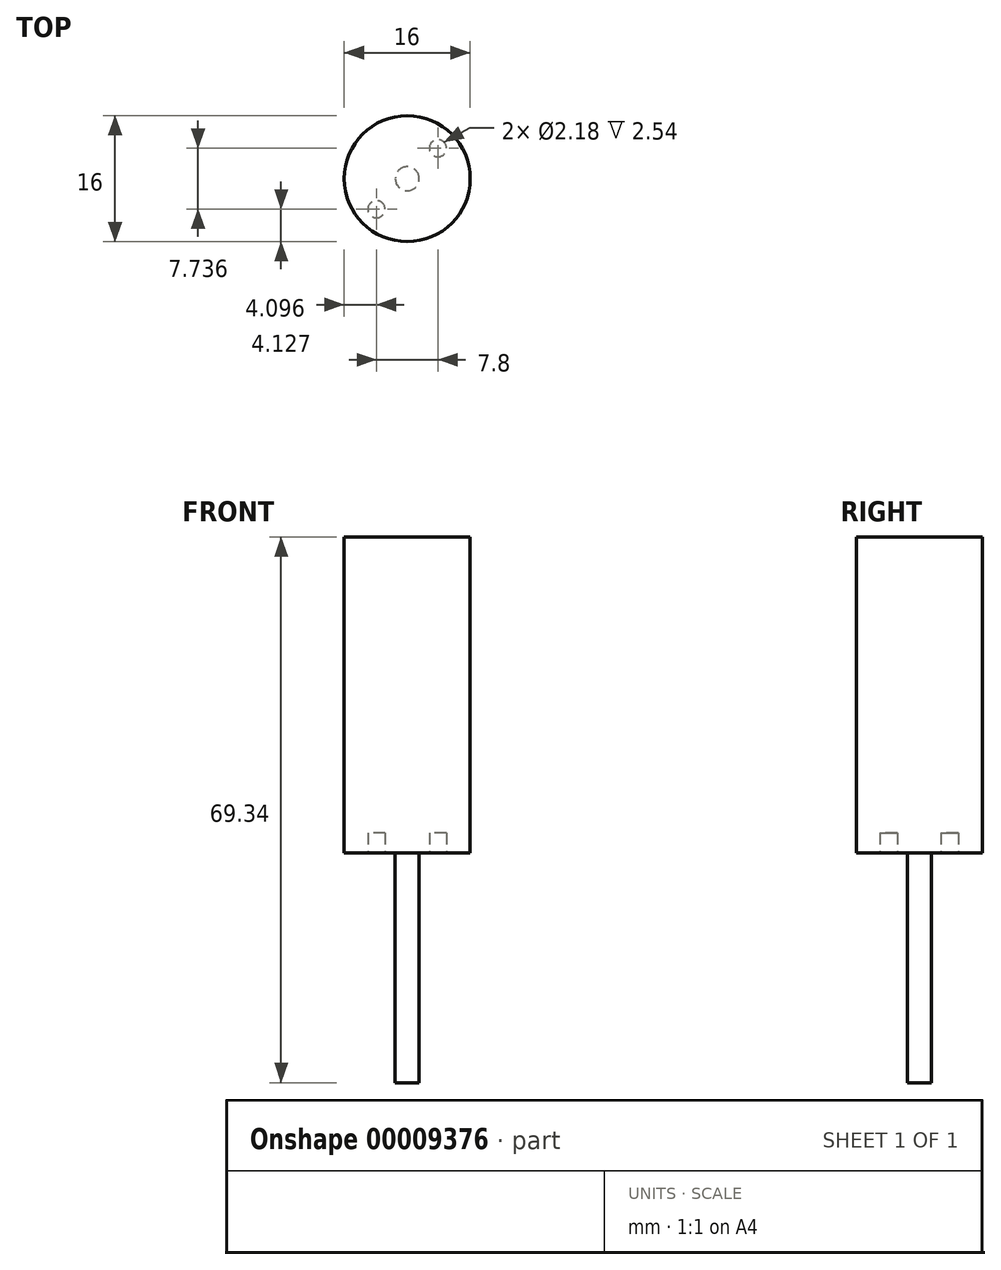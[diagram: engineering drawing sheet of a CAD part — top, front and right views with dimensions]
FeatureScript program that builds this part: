
annotation { "Feature Type Name" : "Feature", "Feature Type Description" : "" }
export const myFeature = defineFeature(function(context is Context, id is Id, definition is map)
    precondition{}
    {
        {
            var Q0;
            Q0=qCreatedBy(makeId("Top.planeOp"),FACE);
            var sketch = newSketch(context, id + "F0", { "sketchPlane" : qUnion([Q0])});
            skCircle(sketch, "E0", {"center": v(0, 0) * mm, "radius": 8 * mm});
            skCircle(sketch, "E1", {"center": v(-3.9, -3.87) * mm, "radius": 1.1 * mm});
            skCircle(sketch, "E2", {"center": v(3.9, 3.86) * mm, "radius": 1.1 * mm});
            skSolve(sketch);
        }
        {
            var Q0;
            Q0=makeQuery(id+"F0.imprint","IMPRINT",FACE,{"disambiguationData":[TD([[makeQuery(id+"F0.imprint","IMPRINT",EDGE,{"derivedFrom":sQuery(id+"F0.wireOp",EDGE,"E1")}),1.0]])]});
            var Q1;
            Q1=makeQuery(id+"F0.imprint","IMPRINT",FACE,{"disambiguationData":[TD([[makeQuery(id+"F0.imprint","IMPRINT",EDGE,{"derivedFrom":sQuery(id+"F0.wireOp",EDGE,"E2")}),1.0]])]});
            var Q2;
            Q2=makeQuery(id+"F0.imprint","IMPRINT",FACE,{"disambiguationData":[TD([[makeQuery(id+"F0.imprint","IMPRINT",EDGE,{"derivedFrom":sQuery(id+"F0.wireOp",EDGE,"E0")}),1.0]])]});
            extrude(context, id + "F1", {"entities" : qUnion([Q0, Q1, Q2]), "depth" : 40.13 * mm});
        }
        {
            var Q0;
            Q0=makeQuery(id+"F0.imprint","IMPRINT",FACE,{"disambiguationData":[TD([[makeQuery(id+"F0.imprint","IMPRINT",EDGE,{"derivedFrom":sQuery(id+"F0.wireOp",EDGE,"E2")}),1.0]])]});
            var Q1;
            Q1=makeQuery(id+"F0.imprint","IMPRINT",FACE,{"disambiguationData":[TD([[makeQuery(id+"F0.imprint","IMPRINT",EDGE,{"derivedFrom":sQuery(id+"F0.wireOp",EDGE,"E1")}),1.0]])]});
            extrude(context, id + "F2", {"entities" : qUnion([Q0, Q1]), "operationType" : NewBodyOperationType.REMOVE, "depth" : 2.54 * mm});
        }
        {
            var Q0;
            Q0=makeQuery(id+"F0.imprint","IMPRINT",FACE,{"disambiguationData":[TD([[makeQuery(id+"F0.imprint","IMPRINT",EDGE,{"derivedFrom":sQuery(id+"F0.wireOp",EDGE,"E0")}),1.0]])]});
            var sketch = newSketch(context, id + "F3", { "sketchPlane" : qUnion([Q0])});
            skCircle(sketch, "E3", {"center": v(0, 0) * mm, "radius": 1.52 * mm});
            skSolve(sketch);
        }
        {
            var Q0;
            Q0=makeQuery(id+"F3.imprint","IMPRINT",FACE,{"disambiguationData":[TD([[makeQuery(id+"F3.imprint","IMPRINT",EDGE,{"derivedFrom":sQuery(id+"F3.wireOp",EDGE,"E3")}),1.0]])]});
            extrude(context, id + "F4", {"entities" : qUnion([Q0]), "operationType" : NewBodyOperationType.ADD, "oppositeDirection" : true, "depth" : 29.2 * mm});
        }
    });
